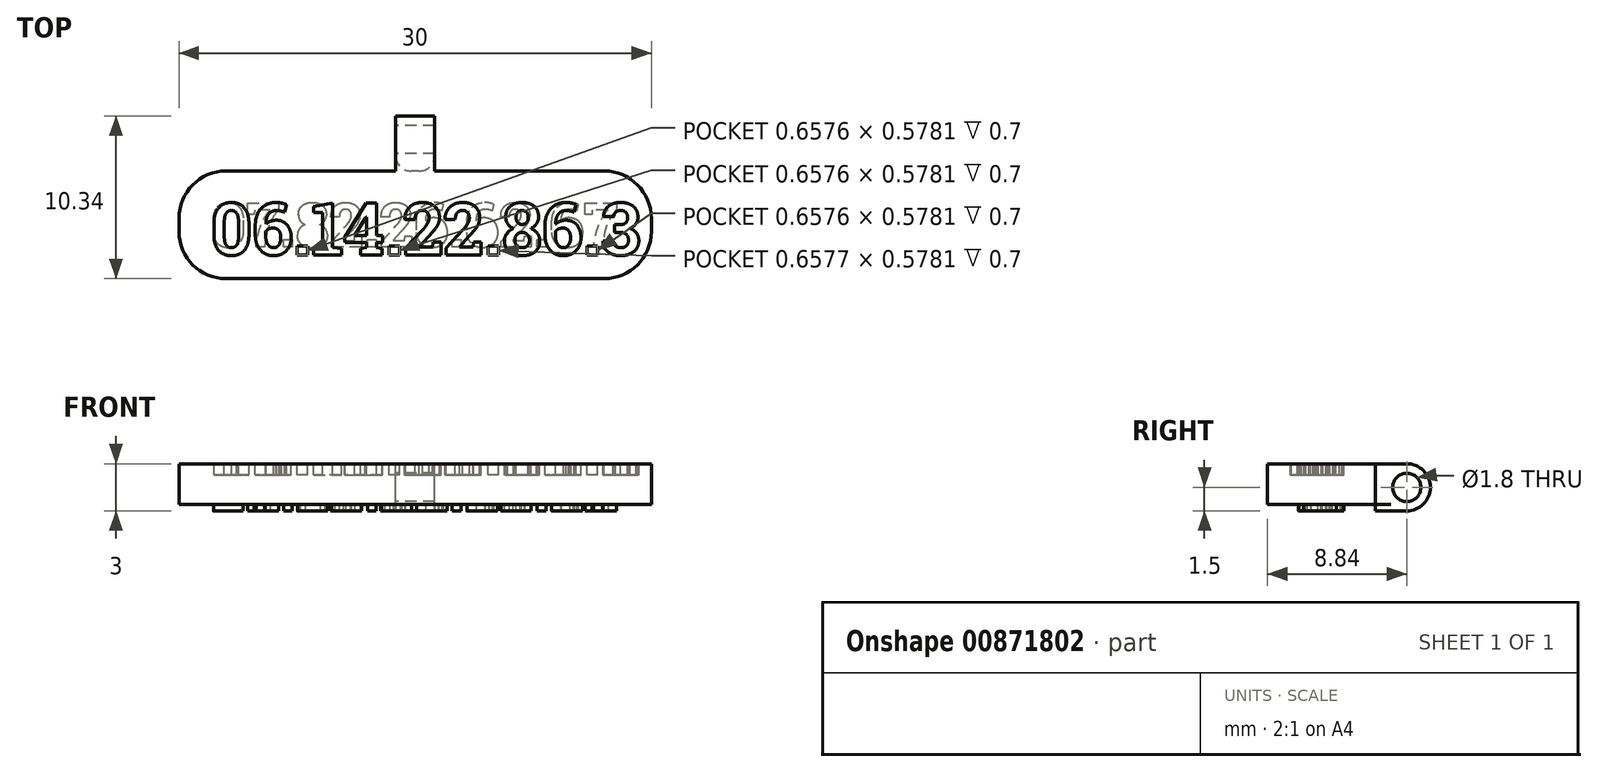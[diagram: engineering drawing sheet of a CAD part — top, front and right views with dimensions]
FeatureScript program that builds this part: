
annotation { "Feature Type Name" : "Feature", "Feature Type Description" : "" }
export const myFeature = defineFeature(function(context is Context, id is Id, definition is map)
    precondition{}
    {
        {
            var Q0;
            Q0=qCreatedBy(makeId("Top.planeOp"),FACE);
            var sketch = newSketch(context, id + "F0", { "sketchPlane" : qUnion([Q0])});
            skText(sketch, "E0", { "text": "07.82.26.62.67", "fontName": "RobotoSlab-Bold.ttf"});
            skLineSegment(sketch, "E1.bottom", {"start": v(28, -4.84) * mm, "end": v(-2, -4.84) * mm});
            skLineSegment(sketch, "E1.top", {"start": v(28, 2) * mm, "end": v(-2, 2) * mm});
            skLineSegment(sketch, "E1.left", {"start": v(28, -4.84) * mm, "end": v(28, 2) * mm});
            skLineSegment(sketch, "E1.right", {"start": v(-2, -4.84) * mm, "end": v(-2, 2) * mm});
            skPoint(sketch, "E1.middle", {"position": v(13, -1.42) * mm});
            const initialGuessF0  = {"E0": [0, -0.00284, 1, 0, 0.00284]};
            skSetInitialGuess(sketch, initialGuessF0);
            skSolve(sketch);
        }
        {
            var Q0;
            Q0=qCreatedBy(makeId("Top.planeOp"),FACE);
            var sketch = newSketch(context, id + "F1", { "sketchPlane" : qUnion([Q0])});
            skLineSegment(sketch, "E2.bottom", {"start": v(-2, 2) * mm, "end": v(28, 2) * mm});
            skLineSegment(sketch, "E2.top", {"start": v(-2, -4.84) * mm, "end": v(28, -4.84) * mm});
            skLineSegment(sketch, "E2.left", {"start": v(-2, 2) * mm, "end": v(-2, -4.84) * mm});
            skLineSegment(sketch, "E2.right", {"start": v(28, 2) * mm, "end": v(28, -4.84) * mm});
            skSolve(sketch);
        }
        {
            var Q0;
            Q0 = qSketchRegion(id + "F1", true);
            extrude(context, id + "F2", {"entities" : qUnion([Q0]), "depth" : 3 * mm, "offsetDistance" : 25 * mm});
        }
        {
            var Q0;
            Q0=makeQuery(id+"F0.imprint","IMPRINT",FACE,{"disambiguationData":[TD([[makeQuery(id+"F0.imprint","IMPRINT",EDGE,{"derivedFrom":sQuery(id+"F0.wireOp",EDGE,"E0.sketch_text.stroke-0")}),1.0]])]});
            var Q1;
            Q1=makeQuery(id+"F0.imprint","IMPRINT",FACE,{"disambiguationData":[TD([[makeQuery(id+"F0.imprint","IMPRINT",EDGE,{"derivedFrom":sQuery(id+"F0.wireOp",EDGE,"E0.sketch_text.stroke-20")}),1.0]])]});
            var Q2;
            Q2=makeQuery(id+"F0.imprint","IMPRINT",FACE,{"disambiguationData":[TD([[makeQuery(id+"F0.imprint","IMPRINT",EDGE,{"derivedFrom":sQuery(id+"F0.wireOp",EDGE,"E0.sketch_text.stroke-37")}),1.0]])]});
            var Q3;
            Q3=makeQuery(id+"F0.imprint","IMPRINT",FACE,{"disambiguationData":[TD([[makeQuery(id+"F0.imprint","IMPRINT",EDGE,{"derivedFrom":sQuery(id+"F0.wireOp",EDGE,"E0.sketch_text.stroke-69")}),1.0]])]});
            var Q4;
            Q4=makeQuery(id+"F0.imprint","IMPRINT",FACE,{"disambiguationData":[TD([[makeQuery(id+"F0.imprint","IMPRINT",EDGE,{"derivedFrom":sQuery(id+"F0.wireOp",EDGE,"E0.sketch_text.stroke-33")}),1.0]])]});
            var Q5;
            Q5=makeQuery(id+"F0.imprint","IMPRINT",FACE,{"disambiguationData":[TD([[makeQuery(id+"F0.imprint","IMPRINT",EDGE,{"derivedFrom":sQuery(id+"F0.wireOp",EDGE,"E0.sketch_text.stroke-92")}),1.0]])]});
            var Q6;
            Q6=makeQuery(id+"F0.imprint","IMPRINT",FACE,{"disambiguationData":[TD([[makeQuery(id+"F0.imprint","IMPRINT",EDGE,{"derivedFrom":sQuery(id+"F0.wireOp",EDGE,"E0.sketch_text.stroke-96")}),1.0]])]});
            var Q7;
            Q7=makeQuery(id+"F0.imprint","IMPRINT",FACE,{"disambiguationData":[TD([[makeQuery(id+"F0.imprint","IMPRINT",EDGE,{"derivedFrom":sQuery(id+"F0.wireOp",EDGE,"E0.sketch_text.stroke-119")}),1.0]])]});
            var Q8;
            Q8=makeQuery(id+"F0.imprint","IMPRINT",FACE,{"disambiguationData":[TD([[makeQuery(id+"F0.imprint","IMPRINT",EDGE,{"derivedFrom":sQuery(id+"F0.wireOp",EDGE,"E0.sketch_text.stroke-151")}),1.0]])]});
            var Q9;
            Q9=makeQuery(id+"F0.imprint","IMPRINT",FACE,{"disambiguationData":[TD([[makeQuery(id+"F0.imprint","IMPRINT",EDGE,{"derivedFrom":sQuery(id+"F0.wireOp",EDGE,"E0.sketch_text.stroke-179")}),1.0]])]});
            var Q10;
            Q10=makeQuery(id+"F0.imprint","IMPRINT",FACE,{"disambiguationData":[TD([[makeQuery(id+"F0.imprint","IMPRINT",EDGE,{"derivedFrom":sQuery(id+"F0.wireOp",EDGE,"E0.sketch_text.stroke-206")}),1.0]])]});
            var Q11;
            Q11=makeQuery(id+"F0.imprint","IMPRINT",FACE,{"disambiguationData":[TD([[makeQuery(id+"F0.imprint","IMPRINT",EDGE,{"derivedFrom":sQuery(id+"F0.wireOp",EDGE,"E0.sketch_text.stroke-234")}),1.0]])]});
            var Q12;
            Q12=makeQuery(id+"F0.imprint","IMPRINT",FACE,{"disambiguationData":[TD([[makeQuery(id+"F0.imprint","IMPRINT",EDGE,{"derivedFrom":sQuery(id+"F0.wireOp",EDGE,"E0.sketch_text.stroke-147")}),1.0]])]});
            var Q13;
            Q13=makeQuery(id+"F0.imprint","IMPRINT",FACE,{"disambiguationData":[TD([[makeQuery(id+"F0.imprint","IMPRINT",EDGE,{"derivedFrom":sQuery(id+"F0.wireOp",EDGE,"E0.sketch_text.stroke-202")}),1.0]])]});
            extrude(context, id + "F3", {"entities" : qUnion([Q0, Q1, Q2, Q3, Q4, Q5, Q6, Q7, Q8, Q9, Q10, Q11, Q12, Q13]), "operationType" : NewBodyOperationType.REMOVE, "depth" : 0.4 * mm, "offsetDistance" : 25 * mm});
        }
        {
            var Q0;
            Q0=makeQuery(id+"F2.opExtrude","CAP_FACE",FACE,{"disambiguationData":[OSD([sQuery(id+"F1.wireOp",EDGE,"E2.bottom"),sQuery(id+"F1.wireOp",EDGE,"E2.top"),sQuery(id+"F1.wireOp",EDGE,"E2.left"),sQuery(id+"F1.wireOp",EDGE,"E2.right")])],"isStart":false});
            var sketch = newSketch(context, id + "F4", { "sketchPlane" : qUnion([Q0])});
            skText(sketch, "E3", { "text": "06.14.22.86.38", "fontName": "RobotoSlab-Bold.ttf"});
            const initialGuessF4  = {"E3": [0, -0.00333, 1, 0, 0.00333]};
            skSetInitialGuess(sketch, initialGuessF4);
            skSolve(sketch);
        }
        {
            var Q0;
            Q0=makeQuery(id+"F4.imprint","IMPRINT",FACE,{"disambiguationData":[TD([[makeQuery(id+"F4.imprint","IMPRINT",EDGE,{"derivedFrom":sQuery(id+"F4.wireOp",EDGE,"E3.sketch_text.stroke-0")}),-1.0]])]});
            var Q1;
            Q1=makeQuery(id+"F4.imprint","IMPRINT",FACE,{"disambiguationData":[TD([[makeQuery(id+"F4.imprint","IMPRINT",EDGE,{"derivedFrom":sQuery(id+"F4.wireOp",EDGE,"E3.sketch_text.stroke-20")}),-1.0]])]});
            var Q2;
            Q2=makeQuery(id+"F4.imprint","IMPRINT",FACE,{"disambiguationData":[TD([[makeQuery(id+"F4.imprint","IMPRINT",EDGE,{"derivedFrom":sQuery(id+"F4.wireOp",EDGE,"E3.sketch_text.stroke-48")}),-1.0]])]});
            var Q3;
            Q3=makeQuery(id+"F4.imprint","IMPRINT",FACE,{"disambiguationData":[TD([[makeQuery(id+"F4.imprint","IMPRINT",EDGE,{"derivedFrom":sQuery(id+"F4.wireOp",EDGE,"E3.sketch_text.stroke-52")}),-1.0]])]});
            var Q4;
            Q4=makeQuery(id+"F4.imprint","IMPRINT",FACE,{"disambiguationData":[TD([[makeQuery(id+"F4.imprint","IMPRINT",EDGE,{"derivedFrom":sQuery(id+"F4.wireOp",EDGE,"E3.sketch_text.stroke-62")}),-1.0]])]});
            var Q5;
            Q5=makeQuery(id+"F4.imprint","IMPRINT",FACE,{"disambiguationData":[TD([[makeQuery(id+"F4.imprint","IMPRINT",EDGE,{"derivedFrom":sQuery(id+"F4.wireOp",EDGE,"E3.sketch_text.stroke-82")}),-1.0]])]});
            var Q6;
            Q6=makeQuery(id+"F4.imprint","IMPRINT",FACE,{"disambiguationData":[TD([[makeQuery(id+"F4.imprint","IMPRINT",EDGE,{"derivedFrom":sQuery(id+"F4.wireOp",EDGE,"E3.sketch_text.stroke-86")}),-1.0]])]});
            var Q7;
            Q7=makeQuery(id+"F4.imprint","IMPRINT",FACE,{"disambiguationData":[TD([[makeQuery(id+"F4.imprint","IMPRINT",EDGE,{"derivedFrom":sQuery(id+"F4.wireOp",EDGE,"E3.sketch_text.stroke-109")}),-1.0]])]});
            var Q8;
            Q8=makeQuery(id+"F4.imprint","IMPRINT",FACE,{"disambiguationData":[TD([[makeQuery(id+"F4.imprint","IMPRINT",EDGE,{"derivedFrom":sQuery(id+"F4.wireOp",EDGE,"E3.sketch_text.stroke-231")}),-1.0]])]});
            var Q9;
            Q9=makeQuery(id+"F4.imprint","IMPRINT",FACE,{"disambiguationData":[TD([[makeQuery(id+"F4.imprint","IMPRINT",EDGE,{"derivedFrom":sQuery(id+"F4.wireOp",EDGE,"E3.sketch_text.stroke-200")}),-1.0]])]});
            var Q10;
            Q10=makeQuery(id+"F4.imprint","IMPRINT",FACE,{"disambiguationData":[TD([[makeQuery(id+"F4.imprint","IMPRINT",EDGE,{"derivedFrom":sQuery(id+"F4.wireOp",EDGE,"E3.sketch_text.stroke-196")}),-1.0]])]});
            var Q11;
            Q11=makeQuery(id+"F4.imprint","IMPRINT",FACE,{"disambiguationData":[TD([[makeQuery(id+"F4.imprint","IMPRINT",EDGE,{"derivedFrom":sQuery(id+"F4.wireOp",EDGE,"E3.sketch_text.stroke-168")}),-1.0]])]});
            var Q12;
            Q12=makeQuery(id+"F4.imprint","IMPRINT",FACE,{"disambiguationData":[TD([[makeQuery(id+"F4.imprint","IMPRINT",EDGE,{"derivedFrom":sQuery(id+"F4.wireOp",EDGE,"E3.sketch_text.stroke-136")}),-1.0]])]});
            var Q13;
            Q13=makeQuery(id+"F4.imprint","IMPRINT",FACE,{"disambiguationData":[TD([[makeQuery(id+"F4.imprint","IMPRINT",EDGE,{"derivedFrom":sQuery(id+"F4.wireOp",EDGE,"E3.sketch_text.stroke-132")}),-1.0]])]});
            extrude(context, id + "F5", {"entities" : qUnion([Q0, Q1, Q2, Q3, Q4, Q5, Q6, Q7, Q8, Q9, Q10, Q11, Q12, Q13]), "operationType" : NewBodyOperationType.REMOVE, "oppositeDirection" : true, "depth" : 0.7 * mm, "offsetDistance" : 25 * mm});
        }
        {
            var Q0;
            Q0=makeQuery(id+"F2.opExtrude","SWEPT_FACE",FACE,{"disambiguationData":[OSD([sQuery(id+"F1.wireOp",EDGE,"E2.right")])]});
            var Q1;
            Q1=makeQuery(id+"F2.opExtrude","SWEPT_FACE",FACE,{"disambiguationData":[OSD([sQuery(id+"F1.wireOp",EDGE,"E2.left")])]});
            cPlane(context, id + "F6", {"entities" : qUnion([Q0, Q1]), "cplaneType" : CPlaneType.MID_PLANE, "offset" : 25 * mm, "width" : 150 * mm, "height" : 150 * mm});
        }
        {
            var Q0;
            Q0=qCreatedBy(id+"F6.planeOp",FACE);
            var sketch = newSketch(context, id + "F7", { "sketchPlane" : qUnion([Q0])});
            skArc(sketch, "E4", {"start": v(4, 0) * mm, "mid": v(5.5, 1.5) * mm, "end": v(4, 3) * mm});
            skCircle(sketch, "E5", {"center": v(4, 1.5) * mm, "radius": 0.9 * mm});
            skLineSegment(sketch, "E6", {"start": v(4, 0) * mm, "end": v(2, 0) * mm});
            skLineSegment(sketch, "E7", {"start": v(4, 3) * mm, "end": v(2, 3) * mm});
            skLineSegment(sketch, "E8", {"start": v(2, 0) * mm, "end": v(2, 3) * mm});
            skSolve(sketch);
        }
        {
            var Q0;
            Q0 = qSketchRegion(id + "F7", true);
            extrude(context, id + "F8", {"entities" : qUnion([Q0]), "operationType" : NewBodyOperationType.ADD, "depth" : 2.5 * mm, "offsetDistance" : 25 * mm, "symmetric" : true});
        }
        {
            var Q0;
            Q0=makeQuery(id+"F2.opExtrude","SWEPT_EDGE",EDGE,{"disambiguationData":[OSD([sQuery(id+"F1.wireOp",EDGE,"E2.bottom"),sQuery(id+"F1.wireOp",EDGE,"E2.right")])]});
            var Q1;
            Q1=makeQuery(id+"F2.opExtrude","SWEPT_EDGE",EDGE,{"disambiguationData":[OSD([sQuery(id+"F1.wireOp",EDGE,"E2.top"),sQuery(id+"F1.wireOp",EDGE,"E2.right")])]});
            var Q2;
            Q2=makeQuery(id+"F2.opExtrude","SWEPT_EDGE",EDGE,{"disambiguationData":[OSD([sQuery(id+"F1.wireOp",EDGE,"E2.bottom"),sQuery(id+"F1.wireOp",EDGE,"E2.left")])]});
            var Q3;
            Q3=makeQuery(id+"F2.opExtrude","SWEPT_EDGE",EDGE,{"disambiguationData":[OSD([sQuery(id+"F1.wireOp",EDGE,"E2.top"),sQuery(id+"F1.wireOp",EDGE,"E2.left")])]});
            fillet(context, id + "F9", {"entities" : qUnion([Q0, Q1, Q2, Q3]), "tangentPropagation" : true, "radius" : 3 * mm, "defaultsChanged" : false, "vertexSettings" : [], "allowEdgeOverflow" : false});
        }
        {
            var Q0;
            Q0=makeQuery(id+"F8.opExtrude","CAP_EDGE",EDGE,{"disambiguationData":[OSD([sQuery(id+"F7.wireOp",EDGE,"E8")])],"isStart":true});
            var Q1;
            Q1=makeQuery(id+"F8.opExtrude","CAP_EDGE",EDGE,{"disambiguationData":[OSD([sQuery(id+"F7.wireOp",EDGE,"E8")])],"isStart":false});
            fillet(context, id + "F10", {"entities" : qUnion([Q0, Q1]), "tangentPropagation" : true, "radius" : 1 * mm, "defaultsChanged" : false, "vertexSettings" : [], "allowEdgeOverflow" : false});
        }
    });
